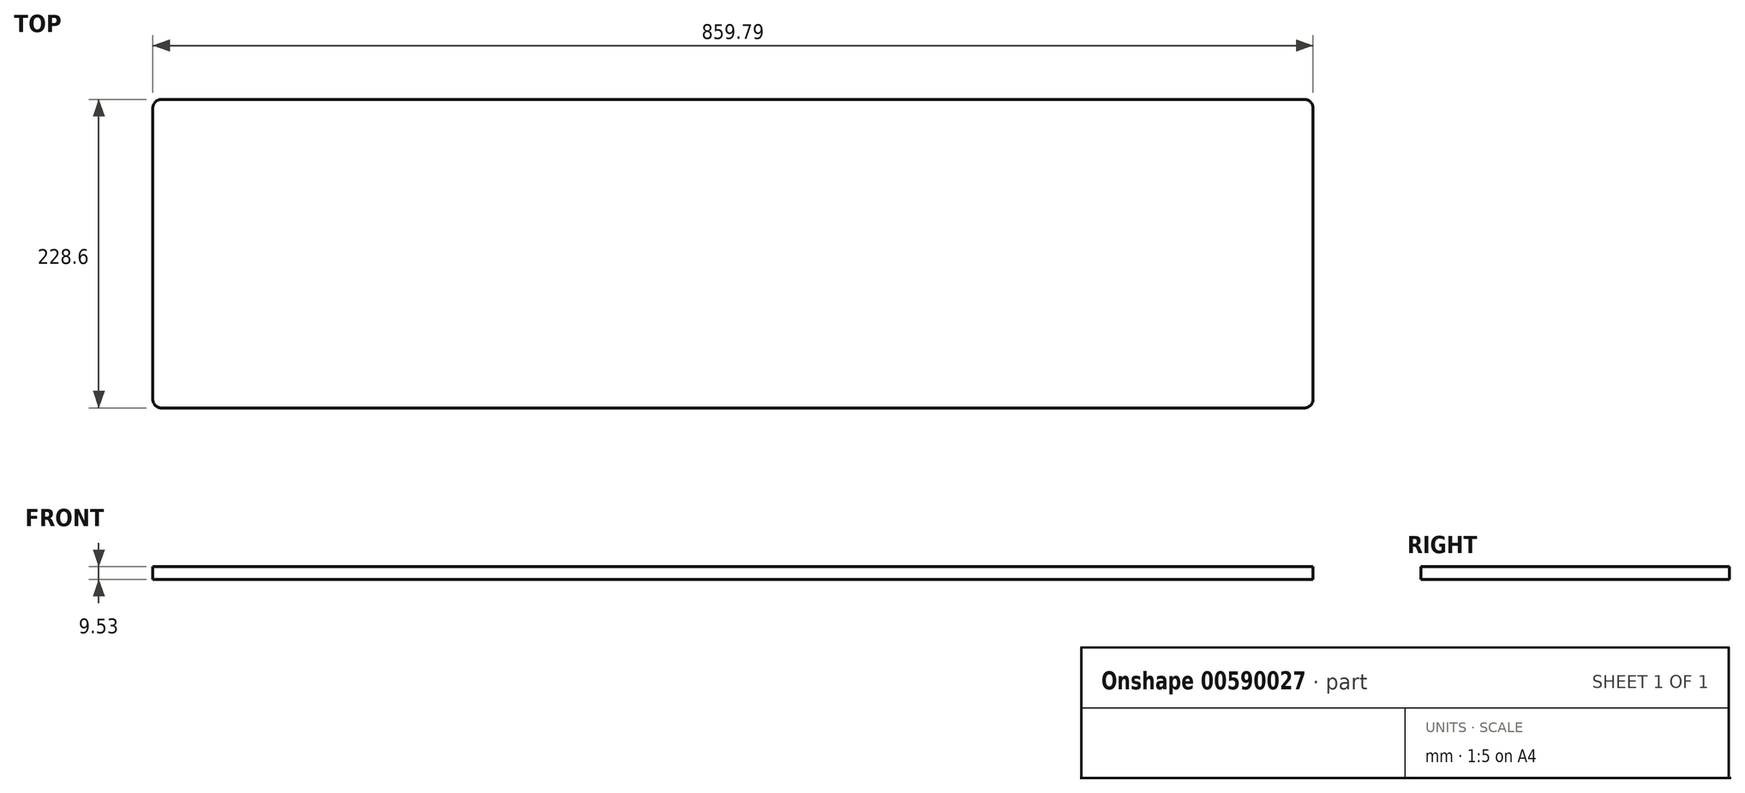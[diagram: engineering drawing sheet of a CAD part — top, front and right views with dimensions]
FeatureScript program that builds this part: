
annotation { "Feature Type Name" : "Feature", "Feature Type Description" : "" }
export const myFeature = defineFeature(function(context is Context, id is Id, definition is map)
    precondition{}
    {
        {
            var Q0;
            Q0=qCreatedBy(makeId("Top.planeOp"),FACE);
            var sketch = newSketch(context, id + "F0", { "sketchPlane" : qUnion([Q0])});
            skLineSegment(sketch, "E0", {"start": v(-403.5, 0) * mm, "end": v(456.3, 0) * mm});
            skLineSegment(sketch, "E1", {"start": v(-403.5, 0) * mm, "end": v(-403.5, 228.6) * mm});
            skLineSegment(sketch, "E2", {"start": v(-403.5, 228.6) * mm, "end": v(456.3, 228.6) * mm});
            skLineSegment(sketch, "E3", {"start": v(456.3, 228.6) * mm, "end": v(456.3, 0) * mm});
            skSolve(sketch);
        }
        {
            var Q0;
            Q0=qSketchRegion(id+"F0",true);
            extrude(context, id + "F1", {"entities" : qUnion([Q0]), "oppositeDirection" : true, "depth" : 9.52 * mm, "offsetDistance" : 25.4 * mm});
        }
        {
            var Q0;
            Q0=makeQuery(id+"F1.opExtrude","SWEPT_EDGE",EDGE,{"disambiguationData":[OSD([sQuery(id+"F0.wireOp",EDGE,"E1"),sQuery(id+"F0.wireOp",EDGE,"E2")])]});
            var Q1;
            Q1=makeQuery(id+"F1.opExtrude","SWEPT_EDGE",EDGE,{"disambiguationData":[OSD([sQuery(id+"F0.wireOp",EDGE,"E0"),sQuery(id+"F0.wireOp",EDGE,"E1")])]});
            var Q2;
            Q2=makeQuery(id+"F1.opExtrude","SWEPT_EDGE",EDGE,{"disambiguationData":[OSD([sQuery(id+"F0.wireOp",EDGE,"E0"),sQuery(id+"F0.wireOp",EDGE,"E3")])]});
            var Q3;
            Q3=makeQuery(id+"F1.opExtrude","SWEPT_EDGE",EDGE,{"disambiguationData":[OSD([sQuery(id+"F0.wireOp",EDGE,"E2"),sQuery(id+"F0.wireOp",EDGE,"E3")])]});
            fillet(context, id + "F2", {"entities" : qUnion([Q0, Q1, Q2, Q3]), "radius" : 6.35 * mm, "tangentPropagation" : true, "allowEdgeOverflow" : false});
        }
    });
